# Revit family: BIMLIB_Шумоглушитель_SCr_SHUFT
name_source: partatom
category: Арматура воздуховодов
revit_build: Autodesk Revit 2017 (Build: 20170118_1100(x64)
units: mm (PartAtom-declared; Revit-internal decimal feet)

## family parameters
Всегда вертикально = Да
На основе рабочей плоскости = Нет
Общий = Нет
При загрузке вырезать с полостями = Нет
Размер круглого соединителя = Использовать диаметр
Тип детали = Вставляется

## types (2) — shared parameters
ADSK_URL документации изделия = http://www.shuft.ru
ADSK_URL страницы изделия = http://www.shuft.ru
ADSK_Версия Revit = 2017
ADSK_Версия семейства = v.1
ADSK_Единица измерения = шт.
ADSK_Завод-изготовитель = ООО «Завод ВКО» марка SHUFT
ADSK_Материал = BIMLIB_Сталь_SHUFT
BL_BIM library = https://bimlib.pro
URL = http://www.shuft.ru
Изготовитель = ООО «Завод ВКО» марка SHUFT
Описание = Шумоглушители серии SCr предназначены для снижения шума от вентилятора в приточных и вытяжных воздуховодах при непосредственной установке в канал систем вентиляции и кондиционирования.

Перемещаемый воздух не должен содержать твердых, клеящихся или агрессивных примесей. Шумоглушители изготавливаются из оцинкованной стали с шумопоглощающим материалом из минерального волокна.
Таблица = SCr

## per-type parameters (varying)
| type | L=600 | L=900 |
| L=600 | Да | Нет |
| L=900 | Нет | Да |
